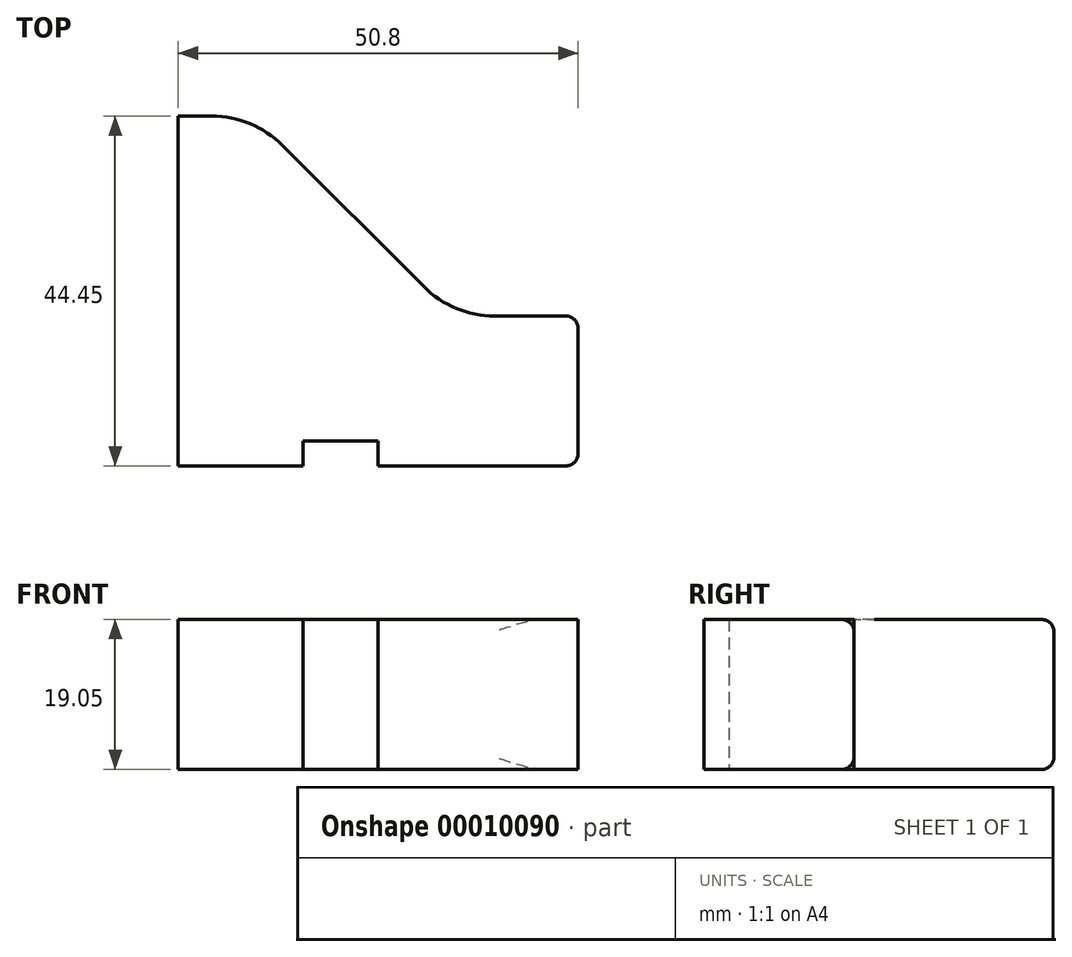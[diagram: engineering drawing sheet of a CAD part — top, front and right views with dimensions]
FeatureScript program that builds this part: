
annotation { "Feature Type Name" : "Feature", "Feature Type Description" : "" }
export const myFeature = defineFeature(function(context is Context, id is Id, definition is map)
    precondition{}
    {
        {
            var Q0;
            Q0=qCreatedBy(makeId("Top.planeOp"),FACE);
            var sketch = newSketch(context, id + "F0", { "sketchPlane" : qUnion([Q0])});
            skLineSegment(sketch, "E0.bottom", {"start": v(0, 0) * mm, "end": v(50.8, 0) * mm});
            skLineSegment(sketch, "E0.top", {"start": v(0, 44.45) * mm, "end": v(4.26, 44.45) * mm});
            skLineSegment(sketch, "E0.left", {"start": v(0, 0) * mm, "end": v(0, 44.45) * mm});
            skLineSegment(sketch, "E0.right", {"start": v(50.8, 0) * mm, "end": v(50.8, 19.05) * mm});
            skLineSegment(sketch, "E1", {"start": v(50.8, 19.05) * mm, "end": v(40.19, 19.05) * mm});
            skLineSegment(sketch, "E2", {"start": v(13.24, 40.73) * mm, "end": v(31.2, 22.77) * mm});
            skPoint(sketch, "E3.visualSharp", {"position": v(34.93, 19.05) * mm});
            skArc(sketch, "E3.filletArc", {"start": v(31.2, 22.77) * mm, "mid": v(35.33, 20.02) * mm, "end": v(40.19, 19.05) * mm});
            skPoint(sketch, "E4.visualSharp", {"position": v(9.52, 44.45) * mm});
            skArc(sketch, "E4.filletArc", {"start": v(13.24, 40.73) * mm, "mid": v(9.12, 43.48) * mm, "end": v(4.26, 44.45) * mm});
            skSolve(sketch);
        }
        {
            var Q0;
            Q0=makeQuery(id+"F0.imprint","IMPRINT",FACE,{"disambiguationData":[TD([[makeQuery(id+"F0.imprint","IMPRINT",EDGE,{"derivedFrom":sQuery(id+"F0.wireOp",EDGE,"E0.bottom")}),1.0]])]});
            extrude(context, id + "F1", {"entities" : qUnion([Q0]), "oppositeDirection" : true, "depth" : 19.05 * mm});
        }
        {
            var Q0;
            Q0=makeQuery(id+"F1.opExtrude","SWEPT_EDGE",EDGE,{"disambiguationData":[OSD([sQuery(id+"F0.wireOp",EDGE,"E0.bottom"),sQuery(id+"F0.wireOp",EDGE,"E0.right")])]});
            var Q1;
            Q1=makeQuery(id+"F1.opExtrude","SWEPT_EDGE",EDGE,{"disambiguationData":[OSD([sQuery(id+"F0.wireOp",EDGE,"E0.right"),sQuery(id+"F0.wireOp",EDGE,"E1")])]});
            fillet(context, id + "F2", {"entities" : qUnion([Q0, Q1]), "radius" : 1.59 * mm, "tangentPropagation" : true, "allowEdgeOverflow" : false});
        }
        {
            var Q0;
            Q0=makeQuery(id+"F1.opExtrude","CAP_EDGE",EDGE,{"disambiguationData":[OSD([sQuery(id+"F0.wireOp",EDGE,"E3.filletArc")])],"isStart":false});
            var Q1;
            Q1=makeQuery(id+"F1.opExtrude","CAP_EDGE",EDGE,{"disambiguationData":[OSD([sQuery(id+"F0.wireOp",EDGE,"E2")])],"isStart":false});
            var Q2;
            Q2=makeQuery(id+"F1.opExtrude","CAP_EDGE",EDGE,{"disambiguationData":[OSD([sQuery(id+"F0.wireOp",EDGE,"E4.filletArc")])],"isStart":false});
            var Q3;
            Q3=makeQuery(id+"F1.opExtrude","CAP_EDGE",EDGE,{"disambiguationData":[OSD([sQuery(id+"F0.wireOp",EDGE,"E0.top")])],"isStart":false});
            fillet(context, id + "F3", {"entities" : qUnion([Q0, Q1, Q2, Q3]), "radius" : 1.59 * mm, "allowEdgeOverflow" : false});
        }
        {
            var Q0;
            Q0=makeQuery(id+"F1.opExtrude","CAP_EDGE",EDGE,{"disambiguationData":[OSD([sQuery(id+"F0.wireOp",EDGE,"E3.filletArc")])],"isStart":true});
            var Q1;
            Q1=makeQuery(id+"F1.opExtrude","CAP_EDGE",EDGE,{"disambiguationData":[OSD([sQuery(id+"F0.wireOp",EDGE,"E2")])],"isStart":true});
            var Q2;
            Q2=makeQuery(id+"F1.opExtrude","CAP_EDGE",EDGE,{"disambiguationData":[OSD([sQuery(id+"F0.wireOp",EDGE,"E0.top")])],"isStart":true});
            fillet(context, id + "F4", {"entities" : qUnion([Q0, Q1, Q2]), "radius" : 1.59 * mm, "allowEdgeOverflow" : false});
        }
        {
            var Q0;
            Q0=makeQuery(id+"F1.opExtrude","SWEPT_FACE",FACE,{"disambiguationData":[OSD([sQuery(id+"F0.wireOp",EDGE,"E0.bottom")])]});
            var sketch = newSketch(context, id + "F5", { "sketchPlane" : qUnion([Q0])});
            skLineSegment(sketch, "E5.bottom", {"start": v(25.4, 0) * mm, "end": v(15.88, 0) * mm});
            skLineSegment(sketch, "E5.top", {"start": v(25.4, -19.05) * mm, "end": v(15.88, -19.05) * mm});
            skLineSegment(sketch, "E5.left", {"start": v(25.4, 0) * mm, "end": v(25.4, -19.05) * mm});
            skLineSegment(sketch, "E5.right", {"start": v(15.88, 0) * mm, "end": v(15.88, -19.05) * mm});
            skSolve(sketch);
        }
        {
            var Q0;
            Q0 = qSketchRegion(id + "F5", true);
            extrude(context, id + "F6", {"entities" : qUnion([Q0]), "operationType" : NewBodyOperationType.REMOVE, "oppositeDirection" : true, "depth" : 3.17 * mm});
        }
    });
